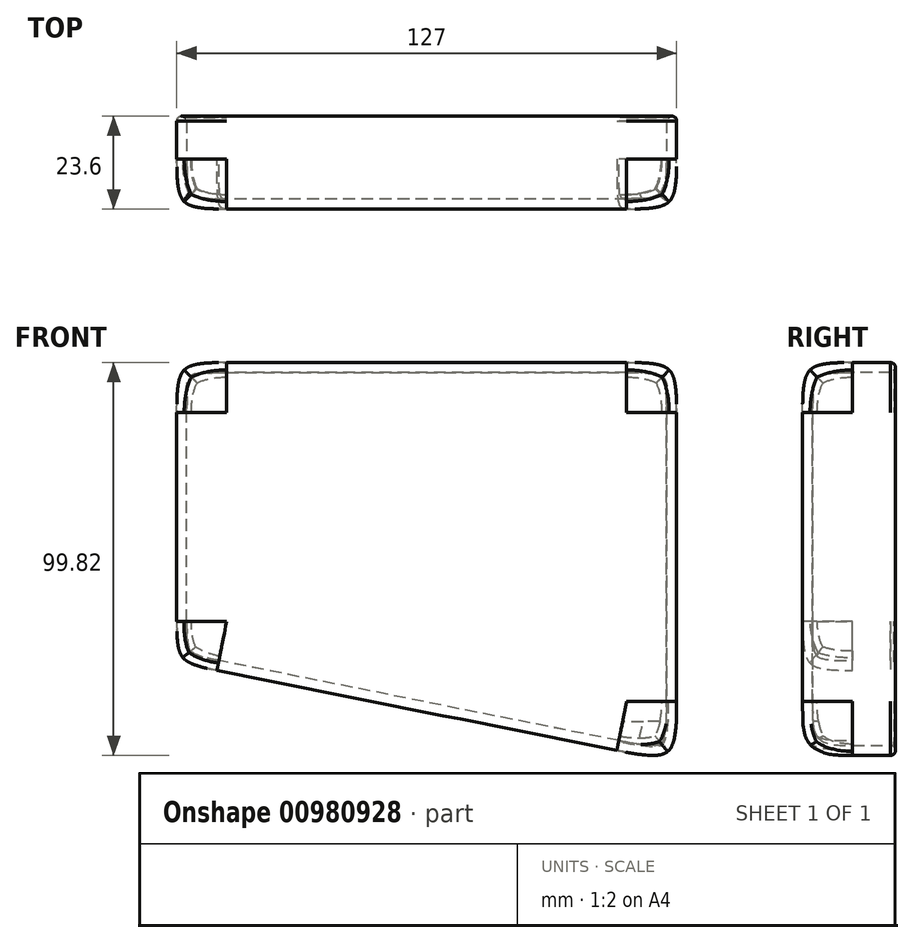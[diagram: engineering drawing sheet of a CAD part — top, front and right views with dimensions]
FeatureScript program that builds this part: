
annotation { "Feature Type Name" : "Feature", "Feature Type Description" : "" }
export const myFeature = defineFeature(function(context is Context, id is Id, definition is map)
    precondition{}
    {
        {
            var Q0;
            Q0=qCreatedBy(makeId("Front.planeOp"),FACE);
            var sketch = newSketch(context, id + "F0", { "sketchPlane" : qUnion([Q0])});
            skLineSegment(sketch, "E0", {"start": v(-66.68, 46.08) * mm, "end": v(-66.68, -30.12) * mm});
            skLineSegment(sketch, "E1", {"start": v(-66.68, 46.08) * mm, "end": v(60.32, 46.08) * mm});
            skLineSegment(sketch, "E2", {"start": v(60.32, 46.08) * mm, "end": v(60.32, 46.08) * mm});
            skLineSegment(sketch, "E3", {"start": v(60.32, 46.08) * mm, "end": v(60.32, -55.52) * mm});
            skLineSegment(sketch, "E4", {"start": v(60.32, -55.52) * mm, "end": v(60.32, -55.52) * mm});
            skLineSegment(sketch, "E5", {"start": v(-66.68, -30.12) * mm, "end": v(60.32, -55.52) * mm});
            skSolve(sketch);
        }
        {
            var Q0;
            Q0=makeQuery(id+"F0.imprint","IMPRINT",FACE,{"disambiguationData":[TD([[makeQuery(id+"F0.imprint","IMPRINT",EDGE,{"derivedFrom":sQuery(id+"F0.wireOp",EDGE,"E0")}),1.0]])]});
            extrude(context, id + "F1", {"entities" : qUnion([Q0]), "depth" : 25.4 * mm, "offsetDistance" : 25.4 * mm});
        }
        {
            var Q0;
            Q0=makeQuery(id+"F1.opExtrude","SWEPT_EDGE",EDGE,{"disambiguationData":[OSD([sQuery(id+"F0.wireOp",EDGE,"E0"),sQuery(id+"F0.wireOp",EDGE,"E5")])]});
            var Q1;
            Q1=makeQuery(id+"F1.opExtrude","CAP_EDGE",EDGE,{"disambiguationData":[OSD([sQuery(id+"F0.wireOp",EDGE,"E5")])],"isStart":false});
            var Q2;
            Q2=makeQuery(id+"F1.opExtrude","CAP_EDGE",EDGE,{"disambiguationData":[OSD([sQuery(id+"F0.wireOp",EDGE,"E0")])],"isStart":false});
            var Q3;
            Q3=makeQuery(id+"F1.opExtrude","SWEPT_EDGE",EDGE,{"disambiguationData":[OSD([sQuery(id+"F0.wireOp",EDGE,"E0"),sQuery(id+"F0.wireOp",EDGE,"E1")])]});
            var Q4;
            Q4=makeQuery(id+"F1.opExtrude","CAP_EDGE",EDGE,{"disambiguationData":[OSD([sQuery(id+"F0.wireOp",EDGE,"E1")])],"isStart":false});
            var Q5;
            Q5=makeQuery(id+"F1.opExtrude","SWEPT_EDGE",EDGE,{"disambiguationData":[OSD([sQuery(id+"F0.wireOp",EDGE,"E1"),sQuery(id+"F0.wireOp",EDGE,"E3")])]});
            var Q6;
            Q6=makeQuery(id+"F1.opExtrude","CAP_EDGE",EDGE,{"disambiguationData":[OSD([sQuery(id+"F0.wireOp",EDGE,"E3")])],"isStart":false});
            var Q7;
            Q7=makeQuery(id+"F1.opExtrude","SWEPT_EDGE",EDGE,{"disambiguationData":[OSD([sQuery(id+"F0.wireOp",EDGE,"E3"),sQuery(id+"F0.wireOp",EDGE,"E5")])]});
            fillet(context, id + "F2", {"entities" : qUnion([Q0, Q1, Q2, Q3, Q4, Q5, Q6, Q7]), "radius" : 12.7 * mm, "tangentPropagation" : true, "rho" : 0.7, "crossSection" : FilletCrossSection.CONIC, "allowEdgeOverflow" : false});
        }
        {
            var Q0;
            Q0=makeQuery(id+"F1.opExtrude","CAP_FACE",FACE,{"disambiguationData":[OSD([sQuery(id+"F0.wireOp",EDGE,"E0"),sQuery(id+"F0.wireOp",EDGE,"E1"),sQuery(id+"F0.wireOp",EDGE,"E3"),sQuery(id+"F0.wireOp",EDGE,"E5")])],"isStart":true});
            shell(context, id + "F3", {"entities" : qUnion([Q0]), "thickness" : 2.54 * mm});
        }
        {
            var Q0;
            {var subQ0=sQuery(id+"F0.wireOp",EDGE,"E5");Q0=makeQuery(id+"F3.opShell","OFFSET_EDGE",EDGE,{"disambiguationData":[OSD([subQ0]),TDD([makeQuery(id+"F1.opExtrude","CAP_EDGE",EDGE,{"disambiguationData":[OSD([subQ0])],"isStart":true})])]});}
            var Q1;
            {var subQ0=sQuery(id+"F0.wireOp",EDGE,"E5");var subQ1=sQuery(id+"F0.wireOp",EDGE,"E3");var subQ2=sQuery(id+"F0.wireOp",EDGE,"E1");var subQ3=sQuery(id+"F0.wireOp",EDGE,"E0");Q1=makeQuery(id+"F3.opShell","OFFSET_EDGE",EDGE,{"disambiguationData":[OSD([subQ3,subQ2,subQ1,subQ0]),TDD([makeQuery(id+"F2.opFillet","BLEND_EDGE",EDGE,{"blendedFrom":[makeQuery(id+"F1.opExtrude","SWEPT_EDGE",EDGE,{"disambiguationData":[OSD([subQ3,subQ0])]}),makeQuery(id+"F1.opExtrude","CAP_FACE",FACE,{"disambiguationData":[OSD([subQ3,subQ2,subQ1,subQ0])],"isStart":true})],"blendedInto":[makeQuery(id+"F1.opExtrude","CAP_FACE",FACE,{"disambiguationData":[OSD([subQ3,subQ2,subQ1,subQ0])],"isStart":true})]})])]});}
            var Q2;
            {var subQ0=sQuery(id+"F0.wireOp",EDGE,"E0");Q2=makeQuery(id+"F3.opShell","OFFSET_EDGE",EDGE,{"disambiguationData":[OSD([subQ0]),TDD([makeQuery(id+"F1.opExtrude","CAP_EDGE",EDGE,{"disambiguationData":[OSD([subQ0])],"isStart":true})])]});}
            var Q3;
            {var subQ0=sQuery(id+"F0.wireOp",EDGE,"E5");var subQ1=sQuery(id+"F0.wireOp",EDGE,"E3");var subQ2=sQuery(id+"F0.wireOp",EDGE,"E1");var subQ3=sQuery(id+"F0.wireOp",EDGE,"E0");Q3=makeQuery(id+"F3.opShell","OFFSET_EDGE",EDGE,{"disambiguationData":[OSD([subQ3,subQ2,subQ1,subQ0]),TDD([makeQuery(id+"F2.opFillet","BLEND_EDGE",EDGE,{"blendedFrom":[makeQuery(id+"F1.opExtrude","SWEPT_EDGE",EDGE,{"disambiguationData":[OSD([subQ3,subQ2])]}),makeQuery(id+"F1.opExtrude","CAP_FACE",FACE,{"disambiguationData":[OSD([subQ3,subQ2,subQ1,subQ0])],"isStart":true})],"blendedInto":[makeQuery(id+"F1.opExtrude","CAP_FACE",FACE,{"disambiguationData":[OSD([subQ3,subQ2,subQ1,subQ0])],"isStart":true})]})])]});}
            var Q4;
            {var subQ0=sQuery(id+"F0.wireOp",EDGE,"E1");Q4=makeQuery(id+"F3.opShell","OFFSET_EDGE",EDGE,{"disambiguationData":[OSD([subQ0]),TDD([makeQuery(id+"F1.opExtrude","CAP_EDGE",EDGE,{"disambiguationData":[OSD([subQ0])],"isStart":true})])]});}
            var Q5;
            {var subQ0=sQuery(id+"F0.wireOp",EDGE,"E5");var subQ1=sQuery(id+"F0.wireOp",EDGE,"E3");var subQ2=sQuery(id+"F0.wireOp",EDGE,"E1");var subQ3=sQuery(id+"F0.wireOp",EDGE,"E0");Q5=makeQuery(id+"F3.opShell","OFFSET_EDGE",EDGE,{"disambiguationData":[OSD([subQ3,subQ2,subQ1,subQ0]),TDD([makeQuery(id+"F2.opFillet","BLEND_EDGE",EDGE,{"blendedFrom":[makeQuery(id+"F1.opExtrude","SWEPT_EDGE",EDGE,{"disambiguationData":[OSD([subQ1,subQ0])]}),makeQuery(id+"F1.opExtrude","CAP_FACE",FACE,{"disambiguationData":[OSD([subQ3,subQ2,subQ1,subQ0])],"isStart":true})],"blendedInto":[makeQuery(id+"F1.opExtrude","CAP_FACE",FACE,{"disambiguationData":[OSD([subQ3,subQ2,subQ1,subQ0])],"isStart":true})]})])]});}
            var Q6;
            {var subQ0=sQuery(id+"F0.wireOp",EDGE,"E3");Q6=makeQuery(id+"F3.opShell","OFFSET_EDGE",EDGE,{"disambiguationData":[OSD([subQ0]),TDD([makeQuery(id+"F1.opExtrude","CAP_EDGE",EDGE,{"disambiguationData":[OSD([subQ0])],"isStart":true})])]});}
            var Q7;
            {var subQ0=sQuery(id+"F0.wireOp",EDGE,"E5");var subQ1=sQuery(id+"F0.wireOp",EDGE,"E3");var subQ2=sQuery(id+"F0.wireOp",EDGE,"E1");var subQ3=sQuery(id+"F0.wireOp",EDGE,"E0");Q7=makeQuery(id+"F3.opShell","OFFSET_EDGE",EDGE,{"disambiguationData":[OSD([subQ3,subQ2,subQ1,subQ0]),TDD([makeQuery(id+"F2.opFillet","BLEND_EDGE",EDGE,{"blendedFrom":[makeQuery(id+"F1.opExtrude","SWEPT_EDGE",EDGE,{"disambiguationData":[OSD([subQ2,subQ1])]}),makeQuery(id+"F1.opExtrude","CAP_FACE",FACE,{"disambiguationData":[OSD([subQ3,subQ2,subQ1,subQ0])],"isStart":true})],"blendedInto":[makeQuery(id+"F1.opExtrude","CAP_FACE",FACE,{"disambiguationData":[OSD([subQ3,subQ2,subQ1,subQ0])],"isStart":true})]})])]});}
            chamfer(context, id + "F4", {"entities" : qUnion([Q0, Q1, Q2, Q3, Q4, Q5, Q6, Q7]), "width" : 2.54 * mm, "tangentPropagation" : true});
        }
        {
            var Q0;
            {var subQ0=sQuery(id+"F0.wireOp",EDGE,"E1");Q0=makeQuery(id+"F4.opChamfer","BLEND_EDGE",EDGE,{"blendedFrom":[makeQuery(id+"F3.opShell","OFFSET_EDGE",EDGE,{"disambiguationData":[OSD([subQ0]),TDD([makeQuery(id+"F1.opExtrude","CAP_EDGE",EDGE,{"disambiguationData":[OSD([subQ0])],"isStart":true})])]}),makeQuery(id+"F1.opExtrude","SWEPT_FACE",FACE,{"disambiguationData":[OSD([subQ0])]})],"blendedInto":[makeQuery(id+"F1.opExtrude","SWEPT_FACE",FACE,{"disambiguationData":[OSD([subQ0])]})]});}
            var Q1;
            {var subQ0=sQuery(id+"F0.wireOp",EDGE,"E1");Q1=makeQuery(id+"F4.opChamfer","BLEND_EDGE",EDGE,{"blendedFrom":[makeQuery(id+"F3.opShell","OFFSET_EDGE",EDGE,{"disambiguationData":[OSD([subQ0]),TDD([makeQuery(id+"F1.opExtrude","CAP_EDGE",EDGE,{"disambiguationData":[OSD([subQ0])],"isStart":true})])]}),makeQuery(id+"F3.opShell","OFFSET_FACE",FACE,{"disambiguationData":[OSD([subQ0]),TDD([makeQuery(id+"F1.opExtrude","SWEPT_FACE",FACE,{"disambiguationData":[OSD([subQ0])]})])]})],"blendedInto":[makeQuery(id+"F3.opShell","OFFSET_FACE",FACE,{"disambiguationData":[OSD([subQ0]),TDD([makeQuery(id+"F1.opExtrude","SWEPT_FACE",FACE,{"disambiguationData":[OSD([subQ0])]})])]})]});}
            fillet(context, id + "F5", {"entities" : qUnion([Q0, Q1]), "radius" : 1.27 * mm, "tangentPropagation" : true, "allowEdgeOverflow" : false});
        }
    });
